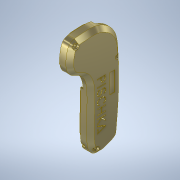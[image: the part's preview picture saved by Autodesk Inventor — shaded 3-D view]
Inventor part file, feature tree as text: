
AUTODESK INVENTOR PART (.ipt)
format: ipt  version: 2020.1 (Build 241239000, 239)  size: 1,641,472 bytes
history: native  units: mm
features: reference x20, extrude x18, sketch x12, other x8, projected_geometry x7, chamfer x6, plane x5, fillet x3, shell x1, emboss x1
ambient origin geometry x8: Origin, YZ Plane, XZ Plane, XY Plane, X Axis, Y Axis, Z Axis, Center Point
bodies: Solid1 (feature_tree)
feature tree (81):
  other  "Outline"
  other  "Acceleration Knob"
  extrude  "Extrusion1"  Depth=33.5mm
  chamfer  "Chamfer1"  Distance=200.0mm Angle=360.0deg
  shell  "Shell1"  Thickness=12.0mm
  extrude  "Extrusion2"  Depth=1.5mm
  plane  "Work Plane1"
  extrude  "Extrusion4"  Depth=4.2mm TaperAngle=0.0deg
  chamfer  "Chamfer2"  Distance=3.2mm
  plane  "Work Plane3"
  sketch  "Sketch8"  dims[d87=31.0mm d88=200.0mm d90=360.0deg d94=12.0mm d95=0.0mm]
  plane  "Work Plane4"
  extrude  "Extrusion5"  Depth=6.4mm
  plane  "Work Plane5"
  extrude  "Extrusion6"  Depth=9.0mm
  extrude  "Extrusion7"  Depth=10.0mm TaperAngle=0.0deg
  extrude  "Extrusion8"  Depth=10.0mm
  extrude  "Extrusion9"  Depth=4.5mm
  chamfer  "Chamfer4"  Distance=4.5mm
  fillet  "Fillet1"  Radius=4.5mm
  fillet  "Fillet2"  Radius=1.5mm
  extrude  "Extrusion10"  Depth=3.5mm
  extrude  "Extrusion11"  Depth=3.5mm
  sketch  "Sketch17"  dims[d113=1.0mm d114=2.0mm d115=45.0deg d119=6.4mm]
  extrude  "Extrusion12"  Depth=3.5mm
  extrude  "Extrusion13"  Depth=10.0mm TaperAngle=0.0deg
  extrude  "Extrusion14"  Depth=4.0mm TaperAngle=0.0deg
  extrude  "Extrusion15"  Depth=10.5mm
  chamfer  "Chamfer5"  Distance=26.2mm
  sketch  "Sketch18"  dims[d121=2.6mm d122=9.0mm]
  extrude  "Extrusion16"  Depth=12.0mm
  extrude  "Extrusion17"  Depth=30.0mm
  chamfer  "Chamfer6"  Distance=3.0mm
  fillet  "Fillet3"  Radius=0.536mm
  emboss  "Emboss1"
  plane  "Work Plane6"
  extrude  "Extrusion18"  Depth=0.5mm
  chamfer  "Chamfer7"  Distance=1.0mm
  extrude  "Extrusion19"  Depth=10.0mm TaperAngle=0.0deg
  other  "Image1"
  sketch  "Sketch5"  dims[d0=131.0mm d86=33.5mm]
  reference  "Reference1"
  reference  "Reference2"
  reference  "Reference3"
  reference  "Reference4"
  reference  "Reference5"
  reference  "Reference6"
  reference  "Reference7"
  sketch  "Sketch9"  dims[d96=4.6mm d97=2.0mm d98=45.0deg d99=1.5mm]
  sketch  "Sketch10"  dims[d103=0.35mm d104=4.2mm d105=0.0mm]
  reference  "Reference8"
  reference  "Reference9"
  reference  "Reference10"
  reference  "Reference11"
  reference  "Reference12"
  reference  "Reference13"
  reference  "Reference14"
  reference  "Reference15"
  reference  "Reference16"
  reference  "Reference17"
  reference  "Reference18"
  reference  "Reference19"
  reference  "Reference20"
  sketch  "Sketch13"  dims[d108=2.6mm]
  sketch  "Sketch15"  dims[d109=6.5mm]
  sketch  "Sketch16"  dims[d110=22.0mm d111=3.2mm d112=0.0mm]
  sketch  "Sketch19"  dims[d123=10.0mm d124=10.0mm d125=0.0mm]
  sketch  "Sketch20"  dims[d126=-3.8mm d127=10.0mm]
  sketch  "Sketch21"  dims[d128=10.0mm d129=0.0mm d130=4.5mm d131=4.5mm d132=4.5mm d133=1.5mm d134=3.5mm d135=3.5mm d136=3.5mm d137=10.0mm d138=0.0mm d139=4.0mm d140=0.0mm d145=10.5mm d146=26.2mm d147=12.0mm d149=30.0mm d150=3.0mm d151=0.0mm d155=0.536mm d156=1.5mm d157=45.0deg d160=0.5mm d161=1.0mm d162=10.0mm d163=0.0mm d164=6.1mm d165=2.55mm d166=0.0mm d167=22.8mm d168=5.8mm d169=7.11mm d170=4.5mm d171=38.0mm d172=3.0mm d173=1.5mm d174=2.0mm d175=1.2mm d176=2.55mm d177=0.0mm d178=1.0mm d179=0.0mm d180=1.0mm d181=0.0mm d182=1.0mm d183=0.0mm d184=1.0mm d185=2.0mm d186=45.0deg d187=12.0mm d188=1.2mm d189=1.2mm d193=2.9mm d194=0.8mm d195=0.8mm d196=0.8mm d197=0.8mm d198=0.8mm d199=1.0mm d200=0.0mm d201=2.0mm d202=0.0mm d203=2.0mm d204=2.0mm d205=45.0deg d206=1.0mm d368=1.0mm d369=0.0mm d371=7.3mm d372=10.0mm d373=1.745329mm d374=3.0mm d375=0.25mm d376=2.0mm d377=45.0deg d378=12.0mm d379=60.0mm d380=56.119884mm d381=28.059942mm d382=0.5mm d383=0.0mm]
  projected_geometry  "Projected Loop1"
  projected_geometry  "Projected Loop2"
  projected_geometry  "Projected Loop3"
  projected_geometry  "Projected Loop4"
  projected_geometry  "Projected Loop5"
  projected_geometry  "Projected Loop6"
  projected_geometry  "Projected Loop7"
  parser-record x1  (decoder bookkeeping rows leaked as tree rows — omitted from the tree; the rows remain in map.json)
  other  "Remote.iam"
  other  "Trigger:1"
  other  "Knob:1"
  other  "Remote Bottom Shell:1"
note: 1 file-system path scrubbed to <path> (originals preserved in map.json)
